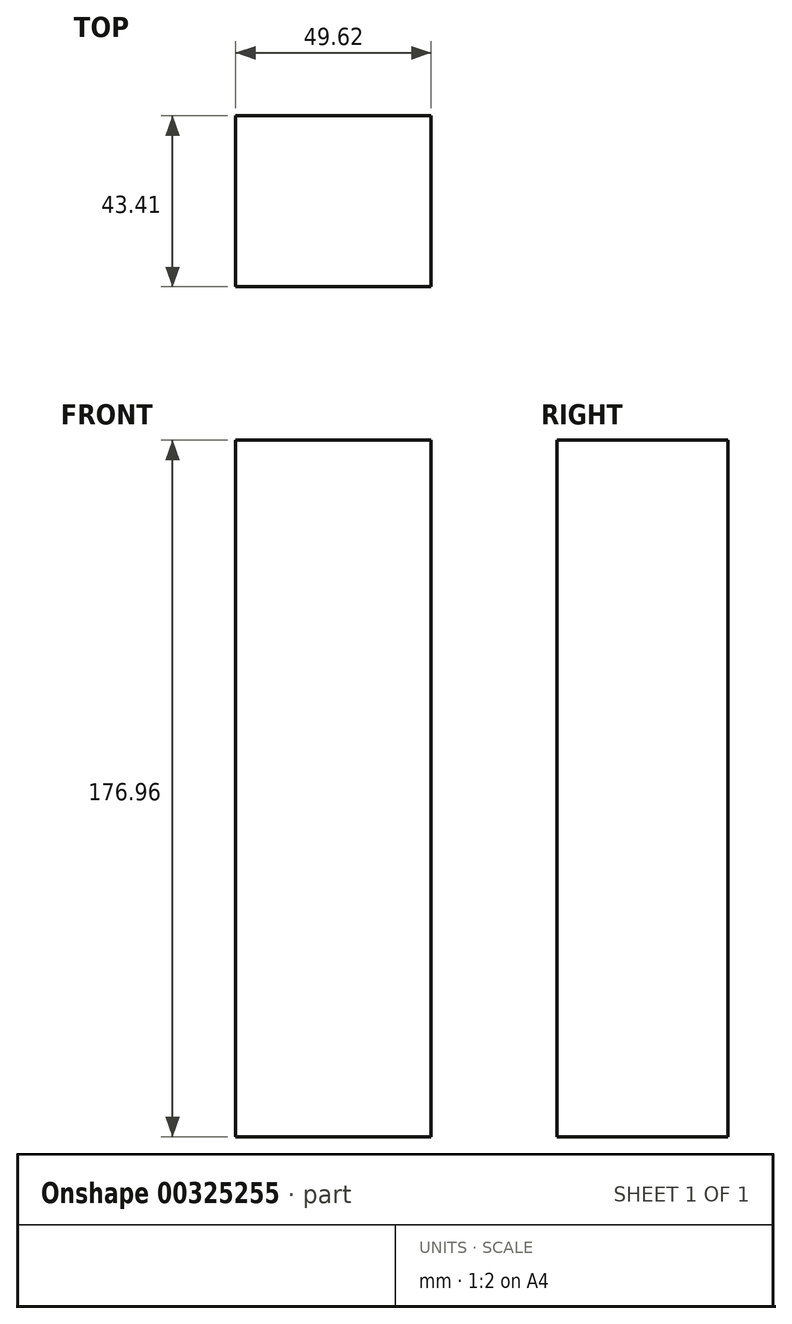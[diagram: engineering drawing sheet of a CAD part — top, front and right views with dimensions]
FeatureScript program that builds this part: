
annotation { "Feature Type Name" : "Feature", "Feature Type Description" : "" }
export const myFeature = defineFeature(function(context is Context, id is Id, definition is map)
    precondition{}
    {
        {
            var Q0;
            Q0=qCreatedBy(makeId("Top.planeOp"),FACE);
            var sketch = newSketch(context, id + "F0", { "sketchPlane" : qUnion([Q0])});
            skLineSegment(sketch, "E0.bottom", {"start": v(-22.14, 18.77) * mm, "end": v(27.48, 18.77) * mm});
            skLineSegment(sketch, "E0.top", {"start": v(-22.14, -24.64) * mm, "end": v(27.48, -24.64) * mm});
            skLineSegment(sketch, "E0.left", {"start": v(-22.14, 18.77) * mm, "end": v(-22.14, -24.64) * mm});
            skLineSegment(sketch, "E0.right", {"start": v(27.48, 18.77) * mm, "end": v(27.48, -24.64) * mm});
            skSolve(sketch);
        }
        {
            var Q0;
            Q0=makeQuery(id+"F0.imprint","IMPRINT",FACE,{"disambiguationData":[TD([[makeQuery(id+"F0.imprint","IMPRINT",EDGE,{"derivedFrom":sQuery(id+"F0.wireOp",EDGE,"E0.bottom")}),-1.0]])]});
            extrude(context, id + "F1", {"entities" : qUnion([Q0]), "depth" : 176.96 * mm});
        }
    });
